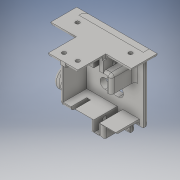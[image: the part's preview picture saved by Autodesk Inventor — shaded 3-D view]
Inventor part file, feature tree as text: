
AUTODESK INVENTOR PART (.ipt)
format: ipt  version: 2016 (Build 200138000, 138)  size: 611,328 bytes
history: native  units: in
note: dims shown in document units (in); Inventor stores cm internally (conversion verified against a paired STEP export)
features: sketch x17, other x3
ambient origin geometry x8: Origin, YZ Plane, XZ Plane, XY Plane, X Axis, Y Axis, Z Axis, Center Point
bodies: Solid1 (feature_tree)
feature tree (20):
  other  "Knee_holder_v3.ipt"
  other  "Solid1::Knee_holder_v3.ipt"
  other  "TaggingFeature1"
  sketch  "Sketch1"  dims[d0=0.3937in]
  sketch  "Sketch12"
  sketch  "Sketch22"
  sketch  "Sketch32"
  sketch  "Sketch35"
  sketch  "Sketch36"
  sketch  "Sketch41"
  sketch  "Sketch43"
  sketch  "Sketch46"
  sketch  "Sketch47"
  sketch  "Sketch48"
  sketch  "Sketch49"
  sketch  "Sketch50"
  sketch  "Sketch51"
  sketch  "Sketch52"
  sketch  "Sketch53"
  sketch  "Sketch54"
